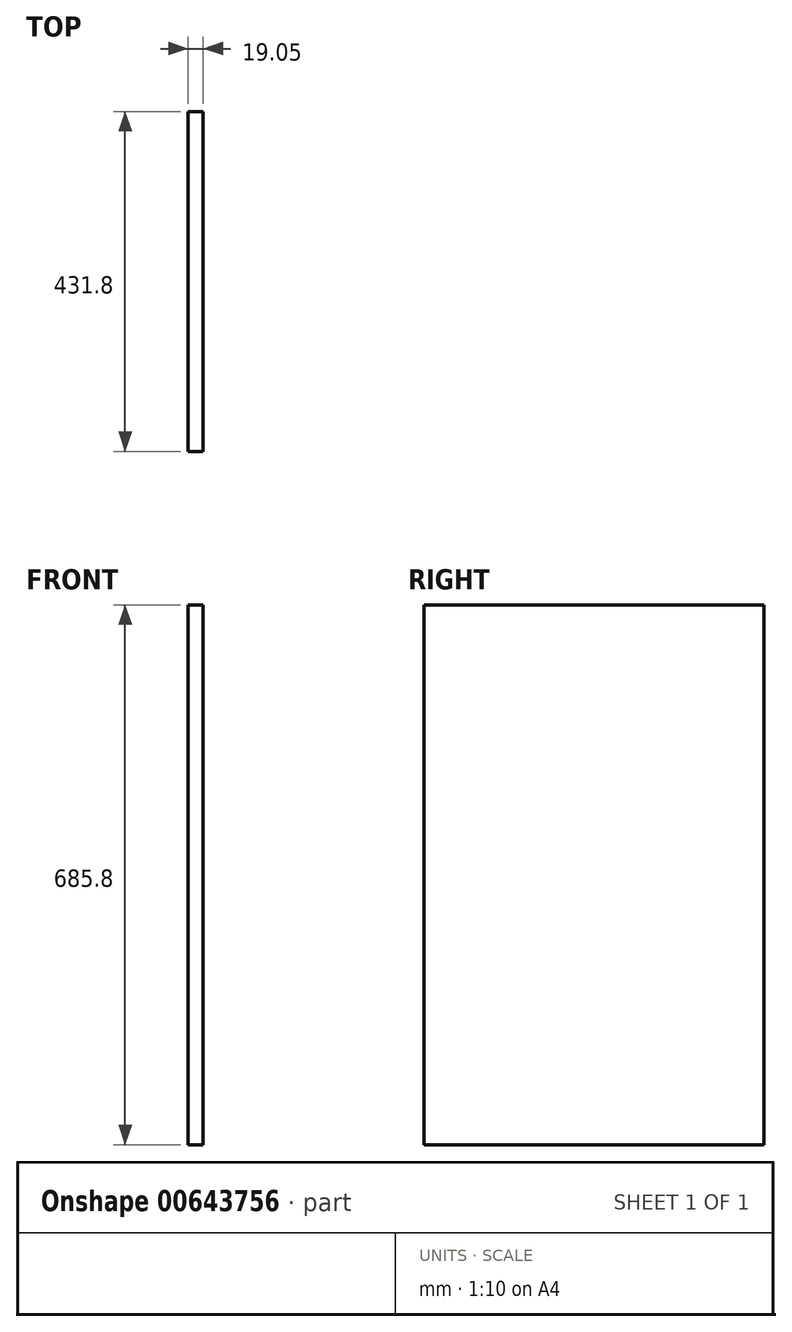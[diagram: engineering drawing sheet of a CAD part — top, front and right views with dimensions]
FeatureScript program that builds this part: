
annotation { "Feature Type Name" : "Feature", "Feature Type Description" : "" }
export const myFeature = defineFeature(function(context is Context, id is Id, definition is map)
    precondition{}
    {
        {
            var Q0;
            Q0=qCreatedBy(makeId("Right.planeOp"),FACE);
            var sketch = newSketch(context, id + "F0", { "sketchPlane" : qUnion([Q0])});
            skLineSegment(sketch, "E0.bottom", {"start": v(0, 0) * mm, "end": v(431.8, 0) * mm});
            skLineSegment(sketch, "E0.top", {"start": v(0, 685.8) * mm, "end": v(431.8, 685.8) * mm});
            skLineSegment(sketch, "E0.left", {"start": v(0, 0) * mm, "end": v(0, 685.8) * mm});
            skLineSegment(sketch, "E0.right", {"start": v(431.8, 0) * mm, "end": v(431.8, 685.8) * mm});
            skSolve(sketch);
        }
        {
            var Q0;
            Q0=makeQuery(id+"F0.imprint","IMPRINT",FACE,{"disambiguationData":[TD([[makeQuery(id+"F0.imprint","IMPRINT",EDGE,{"derivedFrom":sQuery(id+"F0.wireOp",EDGE,"E0.bottom")}),1.0]])]});
            extrude(context, id + "F1", {"entities" : qUnion([Q0]), "depth" : 19.05 * mm, "offsetDistance" : 25.4 * mm});
        }
    });
